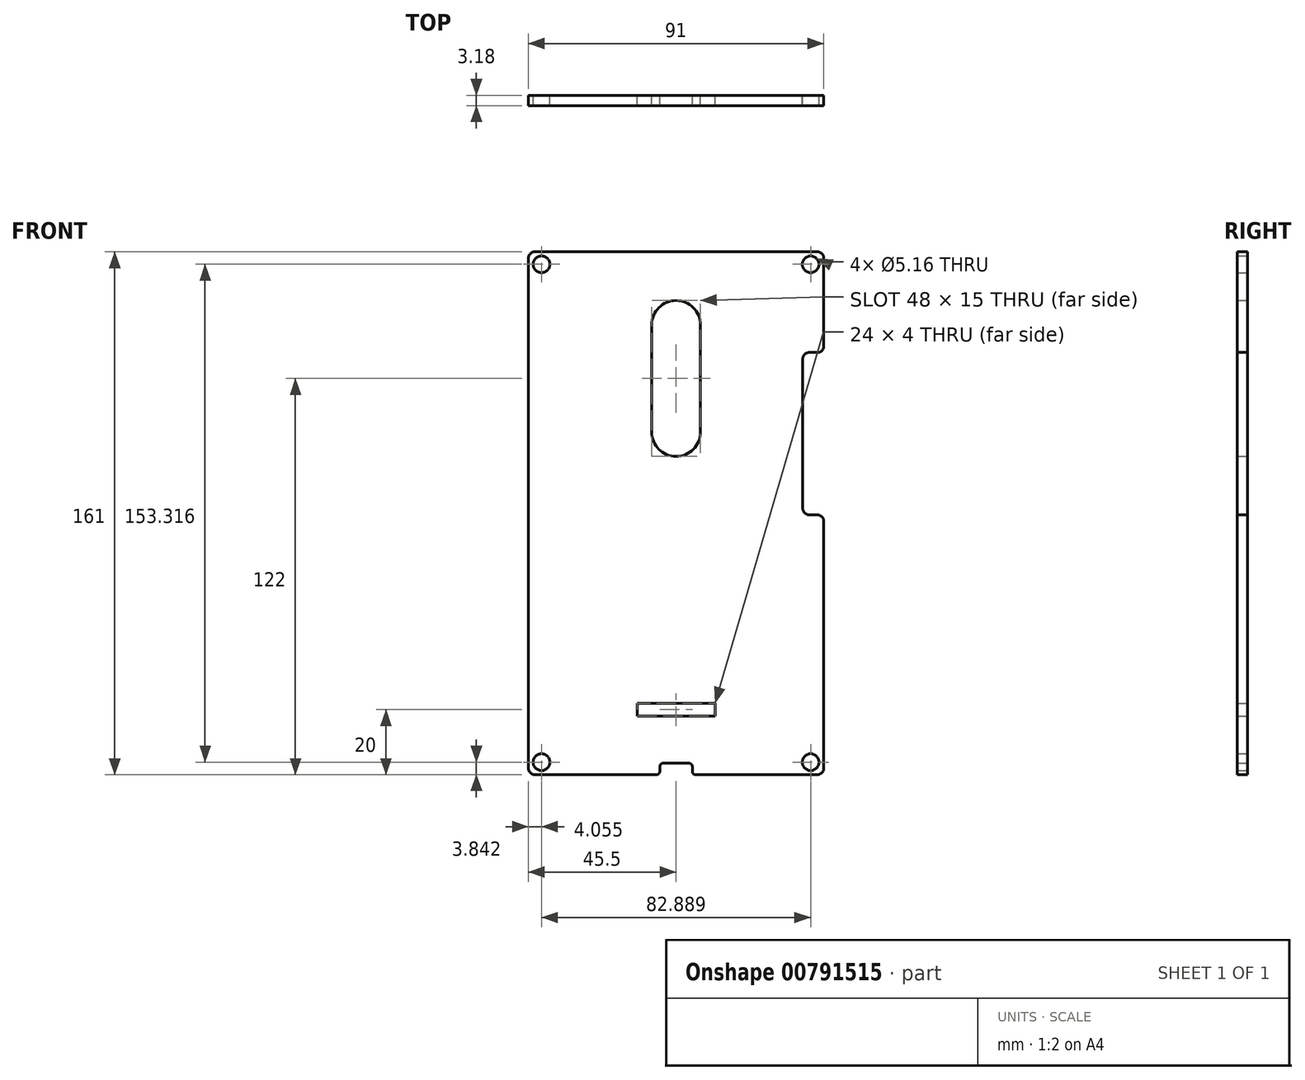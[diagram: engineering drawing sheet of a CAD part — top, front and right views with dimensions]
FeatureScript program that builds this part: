
annotation { "Feature Type Name" : "Feature", "Feature Type Description" : "" }
export const myFeature = defineFeature(function(context is Context, id is Id, definition is map)
    precondition{}
    {
        {
            var Q0;
            Q0=qCreatedBy(makeId("Front.planeOp"),FACE);
            var sketch = newSketch(context, id + "F0", { "sketchPlane" : qUnion([Q0])});
            skLineSegment(sketch, "E0.bottom", {"start": v(39, 74.5) * mm, "end": v(-39, 74.5) * mm});
            skLineSegment(sketch, "E0.top", {"start": v(39, -74.5) * mm, "end": v(-39, -74.5) * mm});
            skLineSegment(sketch, "E0.left", {"start": v(39, 74.5) * mm, "end": v(39, -74.5) * mm});
            skLineSegment(sketch, "E0.right", {"start": v(-39, 74.5) * mm, "end": v(-39, -74.5) * mm});
            skPoint(sketch, "E0.middle", {"position": v(0, 0) * mm});
            skSolve(sketch);
        }
        {
            var Q0;
            Q0=qCreatedBy(makeId("Front.planeOp"),FACE);
            var sketch = newSketch(context, id + "F1", { "sketchPlane" : qUnion([Q0])});
            skPoint(sketch, "E1.middle", {"position": v(0, 0) * mm});
            skLineSegment(sketch, "E2.bottom", {"start": v(45.5, 80.5) * mm, "end": v(-45.5, 80.5) * mm});
            skLineSegment(sketch, "E2.top", {"start": v(45.5, -80.5) * mm, "end": v(5, -80.5) * mm});
            skLineSegment(sketch, "E2.left", {"start": v(45.5, 80.5) * mm, "end": v(45.5, 49.5) * mm});
            skLineSegment(sketch, "E2.right", {"start": v(-45.5, 80.5) * mm, "end": v(-45.5, -80.5) * mm});
            skLineSegment(sketch, "E3", {"start": v(36, 71.5) * mm, "end": v(45.5, 80.5) * mm, "construction": true});
            skLineSegment(sketch, "E4", {"start": v(-36, 71.5) * mm, "end": v(-45.5, 80.5) * mm, "construction": true});
            skLineSegment(sketch, "E5", {"start": v(36, -71.5) * mm, "end": v(45.5, -80.5) * mm, "construction": true});
            skLineSegment(sketch, "E6", {"start": v(-36, -71.5) * mm, "end": v(-45.5, -80.5) * mm, "construction": true});
            skCircle(sketch, "E7", {"center": v(-41.44, 76.66) * mm, "radius": 2.58 * mm});
            skCircle(sketch, "E8", {"center": v(41.44, 76.66) * mm, "radius": 2.58 * mm});
            skCircle(sketch, "E9", {"center": v(41.44, -76.66) * mm, "radius": 2.58 * mm});
            skCircle(sketch, "E10", {"center": v(-41.44, -76.66) * mm, "radius": 2.58 * mm});
            skLineSegment(sketch, "E11.bottom", {"start": v(45.5, 49.5) * mm, "end": v(39, 49.5) * mm});
            skLineSegment(sketch, "E11.top", {"start": v(45.5, -0.5) * mm, "end": v(39, -0.5) * mm});
            skLineSegment(sketch, "E11.right", {"start": v(39, 49.5) * mm, "end": v(39, -0.5) * mm});
            skLineSegment(sketch, "E12.trimOffspring", {"start": v(45.5, -0.5) * mm, "end": v(45.5, -80.5) * mm});
            skLineSegment(sketch, "E13.top", {"start": v(-5, -77) * mm, "end": v(5, -77) * mm});
            skLineSegment(sketch, "E13.left", {"start": v(-5, -80.5) * mm, "end": v(-5, -77) * mm});
            skLineSegment(sketch, "E13.right", {"start": v(5, -80.5) * mm, "end": v(5, -77) * mm});
            skLineSegment(sketch, "E14", {"start": v(0, 0) * mm, "end": v(0, -100.8) * mm, "construction": true});
            skLineSegment(sketch, "E15.trimOffspring", {"start": v(-5, -80.5) * mm, "end": v(-45.5, -80.5) * mm});
            skArc(sketch, "E16", {"start": v(7.5, 58) * mm, "mid": v(0, 65.5) * mm, "end": v(-7.5, 58) * mm});
            skArc(sketch, "E17", {"start": v(-7.5, 25) * mm, "mid": v(0, 17.5) * mm, "end": v(7.5, 25) * mm});
            skLineSegment(sketch, "E18", {"start": v(-7.5, 58) * mm, "end": v(-7.5, 25) * mm});
            skLineSegment(sketch, "E19", {"start": v(7.5, 58) * mm, "end": v(7.5, 25) * mm});
            skLineSegment(sketch, "E20.bottom", {"start": v(12, -58.5) * mm, "end": v(-12, -58.5) * mm});
            skLineSegment(sketch, "E20.top", {"start": v(12, -62.5) * mm, "end": v(-12, -62.5) * mm});
            skLineSegment(sketch, "E20.left", {"start": v(12, -58.5) * mm, "end": v(12, -62.5) * mm});
            skLineSegment(sketch, "E20.right", {"start": v(-12, -58.5) * mm, "end": v(-12, -62.5) * mm});
            skPoint(sketch, "E20.middle", {"position": v(0, -60.5) * mm});
            skSolve(sketch);
        }
        {
            var Q0;
            Q0=qSketchRegion(id+"F1",true);
            extrude(context, id + "F2", {"entities" : qUnion([Q0]), "depth" : 3.17 * mm, "offsetDistance" : 25 * mm});
        }
        {
            var Q0;
            Q0=makeQuery(id+"F2.opExtrude","SWEPT_EDGE",EDGE,{"disambiguationData":[OSD([sQuery(id+"F1.wireOp",EDGE,"E1.bottom"),sQuery(id+"F1.wireOp",EDGE,"E1.right")])]});
            var Q1;
            Q1=makeQuery(id+"F2.opExtrude","SWEPT_EDGE",EDGE,{"disambiguationData":[OSD([sQuery(id+"F1.wireOp",EDGE,"E1.bottom"),sQuery(id+"F1.wireOp",EDGE,"E1.left")])]});
            var Q2;
            Q2=makeQuery(id+"F2.opExtrude","SWEPT_EDGE",EDGE,{"disambiguationData":[OSD([sQuery(id+"F1.wireOp",EDGE,"E2.bottom"),sQuery(id+"F1.wireOp",EDGE,"E2.right")])]});
            var Q3;
            Q3=makeQuery(id+"F2.opExtrude","SWEPT_EDGE",EDGE,{"disambiguationData":[OSD([sQuery(id+"F1.wireOp",EDGE,"E2.bottom"),sQuery(id+"F1.wireOp",EDGE,"E2.left")])]});
            var Q4;
            Q4=makeQuery(id+"F2.opExtrude","SWEPT_EDGE",EDGE,{"disambiguationData":[OSD([sQuery(id+"F1.wireOp",EDGE,"E2.left"),sQuery(id+"F1.wireOp",EDGE,"E11.bottom")])]});
            var Q5;
            Q5=makeQuery(id+"F2.opExtrude","SWEPT_EDGE",EDGE,{"disambiguationData":[OSD([sQuery(id+"F1.wireOp",EDGE,"E11.bottom"),sQuery(id+"F1.wireOp",EDGE,"E11.right")])]});
            var Q6;
            Q6=makeQuery(id+"F2.opExtrude","SWEPT_EDGE",EDGE,{"disambiguationData":[OSD([sQuery(id+"F1.wireOp",EDGE,"E11.top"),sQuery(id+"F1.wireOp",EDGE,"E12.trimOffspring")])]});
            var Q7;
            Q7=makeQuery(id+"F2.opExtrude","SWEPT_EDGE",EDGE,{"disambiguationData":[OSD([sQuery(id+"F1.wireOp",EDGE,"E11.top"),sQuery(id+"F1.wireOp",EDGE,"E11.right")])]});
            var Q8;
            Q8=makeQuery(id+"F2.opExtrude","SWEPT_EDGE",EDGE,{"disambiguationData":[OSD([sQuery(id+"F1.wireOp",EDGE,"E1.top"),sQuery(id+"F1.wireOp",EDGE,"E1.right")])]});
            var Q9;
            Q9=makeQuery(id+"F2.opExtrude","SWEPT_EDGE",EDGE,{"disambiguationData":[OSD([sQuery(id+"F1.wireOp",EDGE,"E2.right"),sQuery(id+"F1.wireOp",EDGE,"E15.trimOffspring")])]});
            var Q10;
            Q10=makeQuery(id+"F2.opExtrude","SWEPT_EDGE",EDGE,{"disambiguationData":[OSD([sQuery(id+"F1.wireOp",EDGE,"E2.top"),sQuery(id+"F1.wireOp",EDGE,"E12.trimOffspring")])]});
            var Q11;
            Q11=makeQuery(id+"F2.opExtrude","SWEPT_EDGE",EDGE,{"disambiguationData":[OSD([sQuery(id+"F1.wireOp",EDGE,"E1.top"),sQuery(id+"F1.wireOp",EDGE,"E1.left")])]});
            fillet(context, id + "F3", {"entities" : qUnion([Q0, Q1, Q2, Q3, Q4, Q5, Q6, Q7, Q8, Q9, Q10, Q11]), "radius" : 2 * mm, "tangentPropagation" : true, "allowEdgeOverflow" : false});
        }
        {
            var Q0;
            Q0=makeQuery(id+"F2.opExtrude","SWEPT_EDGE",EDGE,{"disambiguationData":[OSD([sQuery(id+"F1.wireOp",EDGE,"E2.top"),sQuery(id+"F1.wireOp",EDGE,"E13.right")])]});
            var Q1;
            Q1=makeQuery(id+"F2.opExtrude","SWEPT_EDGE",EDGE,{"disambiguationData":[OSD([sQuery(id+"F1.wireOp",EDGE,"E13.top"),sQuery(id+"F1.wireOp",EDGE,"E13.right")])]});
            var Q2;
            Q2=makeQuery(id+"F2.opExtrude","SWEPT_EDGE",EDGE,{"disambiguationData":[OSD([sQuery(id+"F1.wireOp",EDGE,"E13.top"),sQuery(id+"F1.wireOp",EDGE,"E13.left")])]});
            var Q3;
            Q3=makeQuery(id+"F2.opExtrude","SWEPT_EDGE",EDGE,{"disambiguationData":[OSD([sQuery(id+"F1.wireOp",EDGE,"E13.left"),sQuery(id+"F1.wireOp",EDGE,"E15.trimOffspring")])]});
            fillet(context, id + "F4", {"entities" : qUnion([Q0, Q1, Q2, Q3]), "radius" : 1 * mm, "tangentPropagation" : true, "allowEdgeOverflow" : false});
        }
    });
